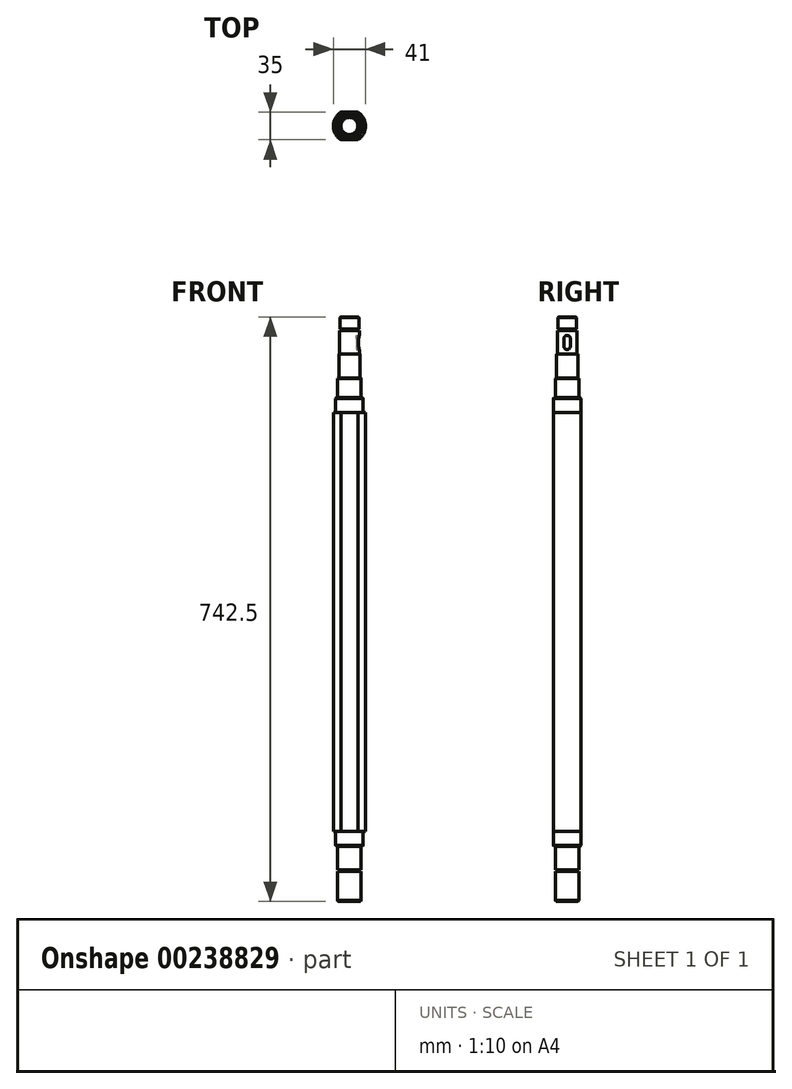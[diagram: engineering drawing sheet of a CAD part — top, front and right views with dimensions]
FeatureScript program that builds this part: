
annotation { "Feature Type Name" : "Feature", "Feature Type Description" : "" }
export const myFeature = defineFeature(function(context is Context, id is Id, definition is map)
    precondition{}
    {
        {
            var Q0;
            Q0=qCreatedBy(makeId("Front.planeOp"),FACE);
            var sketch = newSketch(context, id + "F0", { "sketchPlane" : qUnion([Q0])});
            skLineSegment(sketch, "E0", {"start": v(0, 80.06) * mm, "end": v(0, -667.8) * mm, "construction": true});
            skLineSegment(sketch, "E1", {"start": v(0, 79.07) * mm, "end": v(12, 79.07) * mm});
            skLineSegment(sketch, "E2", {"start": v(12, 79.07) * mm, "end": v(12, 63.57) * mm});
            skLineSegment(sketch, "E3", {"start": v(12, 63.57) * mm, "end": v(10, 63.57) * mm});
            skLineSegment(sketch, "E4", {"start": v(10, 63.57) * mm, "end": v(10, 61.57) * mm});
            skLineSegment(sketch, "E5", {"start": v(10, 61.57) * mm, "end": v(12.5, 61.57) * mm});
            skLineSegment(sketch, "E6", {"start": v(12.5, 61.57) * mm, "end": v(12.5, 31.57) * mm});
            skLineSegment(sketch, "E7", {"start": v(12.5, 31.57) * mm, "end": v(13.5, 31.57) * mm});
            skLineSegment(sketch, "E8", {"start": v(13.5, 31.57) * mm, "end": v(13.5, 1.57) * mm});
            skLineSegment(sketch, "E9", {"start": v(13.5, 1.57) * mm, "end": v(15, 1.57) * mm});
            skLineSegment(sketch, "E10", {"start": v(15, 1.57) * mm, "end": v(15, -23.43) * mm});
            skLineSegment(sketch, "E11", {"start": v(15, -23.43) * mm, "end": v(17.5, -23.43) * mm});
            skLineSegment(sketch, "E12", {"start": v(17.5, -23.43) * mm, "end": v(17.5, -42.43) * mm});
            skLineSegment(sketch, "E13", {"start": v(17.5, -42.43) * mm, "end": v(20.5, -42.43) * mm});
            skLineSegment(sketch, "E14", {"start": v(20.5, -42.43) * mm, "end": v(20.5, -574.43) * mm});
            skLineSegment(sketch, "E15", {"start": v(20.5, -574.43) * mm, "end": v(17.5, -574.43) * mm});
            skLineSegment(sketch, "E16", {"start": v(17.5, -574.43) * mm, "end": v(17.5, -593.43) * mm});
            skLineSegment(sketch, "E17", {"start": v(17.5, -593.43) * mm, "end": v(15, -593.43) * mm});
            skLineSegment(sketch, "E18", {"start": v(15, -593.43) * mm, "end": v(15, -623.43) * mm});
            skLineSegment(sketch, "E19", {"start": v(15, -623.43) * mm, "end": v(13, -623.43) * mm});
            skLineSegment(sketch, "E20", {"start": v(13, -623.43) * mm, "end": v(13, -625.43) * mm});
            skLineSegment(sketch, "E21", {"start": v(13, -625.43) * mm, "end": v(15, -625.43) * mm});
            skLineSegment(sketch, "E22", {"start": v(15, -625.43) * mm, "end": v(15, -663.43) * mm});
            skLineSegment(sketch, "E23", {"start": v(15, -663.43) * mm, "end": v(0, -663.43) * mm});
            skLineSegment(sketch, "E24", {"start": v(0, 79.07) * mm, "end": v(0, -663.43) * mm});
            skSolve(sketch);
        }
        {
            var Q0;
            Q0=makeQuery(id+"F0.imprint","IMPRINT",FACE,{"disambiguationData":[TD([[makeQuery(id+"F0.imprint","IMPRINT",EDGE,{"derivedFrom":sQuery(id+"F0.wireOp",EDGE,"E1")}),-1.0]])]});
            var Q1;
            Q1=sQuery(id+"F0.wireOp",EDGE,"E24");
            revolve(context, id + "F1", {"entities" : qUnion([Q0]), "axis" : qUnion([Q1]), "revolveType" : RevolveType.FULL});
        }
        {
            var Q0;
            Q0=makeQuery(id+"F1.opRevolve","SWEPT_FACE",FACE,{"disambiguationData":[OSD([sQuery(id+"F0.wireOp",EDGE,"E13")])]});
            var sketch = newSketch(context, id + "F2", { "sketchPlane" : qUnion([Q0])});
            skLineSegment(sketch, "E25", {"start": v(-10.68, 17.5) * mm, "end": v(10.68, 17.5) * mm});
            skArc(sketch, "E26", {"start": v(10.68, 17.5) * mm, "mid": v(0, 22.16) * mm, "end": v(-10.68, 17.5) * mm});
            skLineSegment(sketch, "E27", {"start": v(-10.68, -17.5) * mm, "end": v(10.68, -17.5) * mm});
            skArc(sketch, "E28", {"start": v(-10.68, -17.5) * mm, "mid": v(0, -22) * mm, "end": v(10.68, -17.5) * mm});
            skSolve(sketch);
        }
        {
            var Q0;
            {var subQ1=sQuery(id+"F2.wireOp",EDGE,"E25");var subQ2=sQuery(id+"F0.wireOp",EDGE,"E13");var subQ5=makeQuery(id+"F2.imprint","INTERSECT",VERTEX,{"derivedFrom":[makeQuery(id+"F1.opRevolve","SWEPT_EDGE",EDGE,{"disambiguationData":[OSD([sQuery(id+"F0.wireOp",EDGE,"E12"),subQ2])]}),subQ1]});Q0=makeQuery(id+"F2.imprint","IMPRINT",FACE,{"disambiguationData":[TD([[makeQuery(id+"F2.imprint","IMPRINT",EDGE,{"disambiguationData":[TD([[subQ5,1.0]])],"derivedFrom":subQ1}),1.0]])]});}
            var Q1;
            {var subQ1=sQuery(id+"F2.wireOp",EDGE,"E27");var subQ2=sQuery(id+"F0.wireOp",EDGE,"E13");var subQ5=makeQuery(id+"F2.imprint","INTERSECT",VERTEX,{"derivedFrom":[makeQuery(id+"F1.opRevolve","SWEPT_EDGE",EDGE,{"disambiguationData":[OSD([sQuery(id+"F0.wireOp",EDGE,"E12"),subQ2])]}),subQ1]});Q1=makeQuery(id+"F2.imprint","IMPRINT",FACE,{"disambiguationData":[TD([[makeQuery(id+"F2.imprint","IMPRINT",EDGE,{"disambiguationData":[TD([[subQ5,1.0]])],"derivedFrom":subQ1}),-1.0]])]});}
            extrude(context, id + "F3", {"entities" : qUnion([Q0, Q1]), "operationType" : NewBodyOperationType.REMOVE, "endBound" : BoundingType.THROUGH_ALL, "oppositeDirection" : true, "depth" : 25 * mm});
        }
        {
            var Q0;
            Q0=makeQuery(id+"F1.opRevolve","SWEPT_EDGE",EDGE,{"disambiguationData":[OSD([sQuery(id+"F0.wireOp",EDGE,"E22"),sQuery(id+"F0.wireOp",EDGE,"E23")])]});
            var Q1;
            Q1=makeQuery(id+"F1.opRevolve","SWEPT_EDGE",EDGE,{"disambiguationData":[OSD([sQuery(id+"F0.wireOp",EDGE,"E16"),sQuery(id+"F0.wireOp",EDGE,"E17")])]});
            var Q2;
            Q2=makeQuery(id+"F1.opRevolve","SWEPT_EDGE",EDGE,{"disambiguationData":[OSD([sQuery(id+"F0.wireOp",EDGE,"E1"),sQuery(id+"F0.wireOp",EDGE,"E2")])]});
            var Q3;
            Q3=makeQuery(id+"F1.opRevolve","SWEPT_EDGE",EDGE,{"disambiguationData":[OSD([sQuery(id+"F0.wireOp",EDGE,"E9"),sQuery(id+"F0.wireOp",EDGE,"E10")])]});
            var Q4;
            Q4=makeQuery(id+"F1.opRevolve","SWEPT_EDGE",EDGE,{"disambiguationData":[OSD([sQuery(id+"F0.wireOp",EDGE,"E11"),sQuery(id+"F0.wireOp",EDGE,"E12")])]});
            chamfer(context, id + "F4", {"entities" : qUnion([Q0, Q1, Q2, Q3, Q4]), "width" : 1 * mm, "tangentPropagation" : true});
        }
        {
            var Q0;
            Q0=qCreatedBy(makeId("Right.planeOp"),FACE);
            cPlane(context, id + "F5", {"entities" : qUnion([Q0]), "cplaneType" : CPlaneType.OFFSET, "offset" : 15 * mm, "width" : 150 * mm, "height" : 150 * mm});
        }
        {
            var Q0;
            Q0=qCreatedBy(id+"F5.planeOp",FACE);
            var sketch = newSketch(context, id + "F6", { "sketchPlane" : qUnion([Q0])});
            skLineSegment(sketch, "E29.left", {"start": v(-4, 51.57) * mm, "end": v(-4, 41.57) * mm});
            skLineSegment(sketch, "E29.right", {"start": v(4, 51.57) * mm, "end": v(4, 41.57) * mm});
            skArc(sketch, "E30", {"start": v(4, 51.57) * mm, "mid": v(0, 55.57) * mm, "end": v(-4, 51.57) * mm});
            skArc(sketch, "E31", {"start": v(-4, 41.57) * mm, "mid": v(0, 37.57) * mm, "end": v(4, 41.57) * mm});
            skLineSegment(sketch, "E32", {"start": v(0, 46.2) * mm, "end": v(0, 18.5) * mm, "construction": true});
            skLineSegment(sketch, "E33", {"start": v(-4, 41.57) * mm, "end": v(4, 41.57) * mm, "construction": true});
            skLineSegment(sketch, "E34", {"start": v(-4, 51.57) * mm, "end": v(4, 51.57) * mm, "construction": true});
            skSolve(sketch);
        }
        {
            var Q0;
            Q0=makeQuery(id+"F6.imprint","IMPRINT",FACE,{"disambiguationData":[TD([[makeQuery(id+"F6.imprint","IMPRINT",EDGE,{"derivedFrom":sQuery(id+"F6.wireOp",EDGE,"E29.left")}),1.0]])]});
            extrude(context, id + "F7", {"entities" : qUnion([Q0]), "operationType" : NewBodyOperationType.REMOVE, "oppositeDirection" : true, "depth" : 6 * mm});
        }
    });
